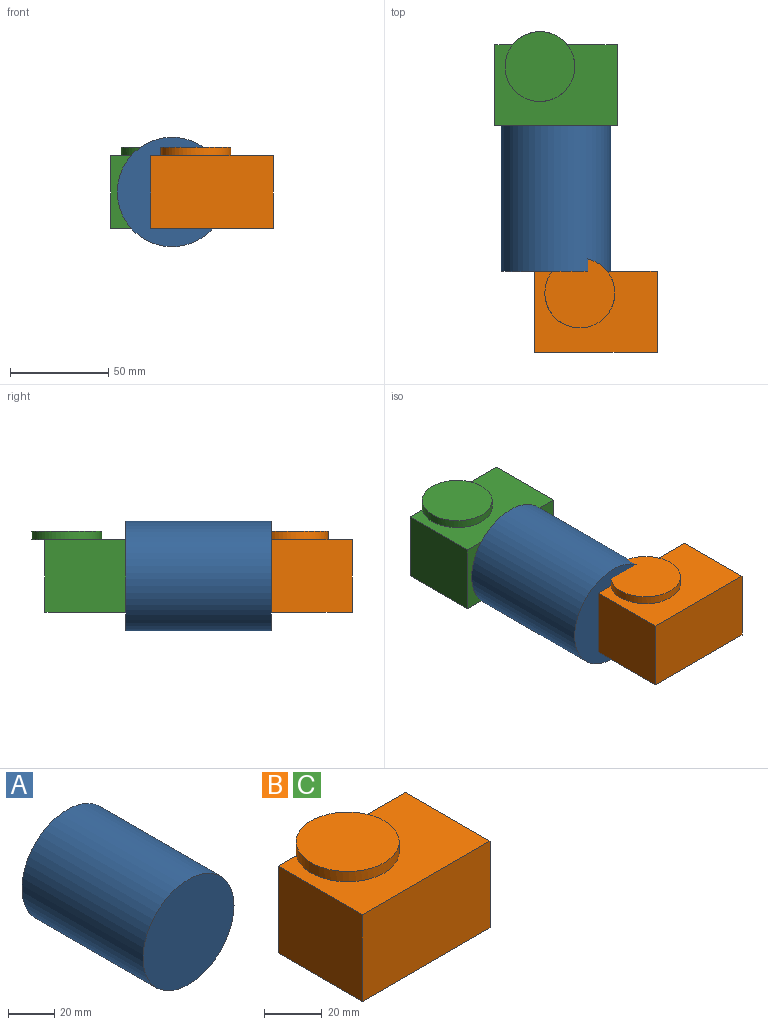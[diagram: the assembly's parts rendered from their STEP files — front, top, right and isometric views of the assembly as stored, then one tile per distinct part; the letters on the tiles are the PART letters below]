
ASSEMBLY  parts=3 mates=2
PART A: 3 faces, bbox 55.7x74.2x55.7 mm
  f0: cylinder r=27.87mm len=74.17mm, axis (0,1,0), area 12988.1mm2, adj f1,f2
  f1: plane 55.74x55.74mm, normal (0,-1,0), area 2440.3mm2, adj f0
  f2: plane 55.74x55.74mm, normal (0,1,0), area 2440.3mm2, adj f0
PART B: 9 faces, bbox 62.3x47.9x41 mm
  f0: plane 41.15x36.69mm, normal (-1,0,0), area 1509.7mm2, adj f1,f3,f4,f5
  f1: plane 62.29x41.15mm, normal (0,0,-1), area 2562.9mm2, adj f0,f2,f4,f5
  f2: plane 41.15x36.69mm, normal (1,0,0), area 1509.7mm2, adj f1,f3,f4,f5
  f3: plane 62.29x41.15mm, normal (0,0,1), area 1701mm2, adj f0,f2,f4,f5,f6
  f4: plane 62.29x36.69mm, normal (0,-1,0), area 2285.2mm2, adj f0,f1,f2,f3
  f5: plane 62.29x36.69mm, normal (0,1,0), area 2285.2mm2, adj f0,f1,f2,f3,f8
  f6: cylinder r=17.78mm len=35.56mm, axis (0,0,-1), area 482.4mm2, adj f3,f7,f8
  f7: plane 35.56x35.56mm, normal (0,0,1), area 993.1mm2, adj f6
  f8: plane 27.89x6.75mm, normal (0,0,-1), area 131.2mm2, adj f5,f6
PART C: same geometry as B
PLACE A t=(61.69,120.72,60.01)mm
PLACE B t=(113.15,46.56,35.5)mm
PLACE C t=(92.83,161.87,35.5)mm
MATE fastened A.f1 <-> B.f5  axis (0,-1,0) through (82.01,46.56,60.01)mm
MATE fastened A.f0 <-> C.f4  axis (0,1,0) through (61.69,120.72,60.01)mm
